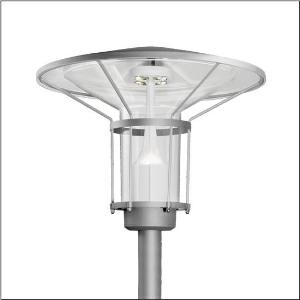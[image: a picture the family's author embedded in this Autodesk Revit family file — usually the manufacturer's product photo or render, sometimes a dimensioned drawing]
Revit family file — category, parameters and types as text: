
# Revit family: laterne_classic_iq___pl1_2s_5xa5245of14h_0553
name_source: partatom
category: Lighting Fixtures
units: mm (PartAtom-declared; Revit-internal decimal feet)

## family parameters
Cut with Voids When Loaded = No
Host = Face
Light Source = No
Part Type = Normal
Room Calculation Point = No
Round Connector Dimension = Use Diameter
Shared = No

## types (1)
- --- (1 x LED, 2670 lm, 21.8 W, 2700K)
    Apparent Load = 22 VA
    CIE Flux Codes = 21 60 93 97 100
    Color Rendering = 70
    Color Temperature = 2700K
    Default Elevation = 1800 mm
    Description = Lantern Classic iQ, mast luminaire, Module 540 iQ-SR, primary light control with 3 zone facetted reflector, of plastic, silver coated, highly specular, structured, primary optical cover: cover, of PMMA, transparent, light distribution: PL1.2s, light emission: direct distribution, primary light characteristic: symmetric, installation type: post-top, LED, High Power LED, rated luminous flux: 2.970lm, luminous efficacy: 136lm/W, light colour: 727, colour temperature: 2700K, control gear: ECG iQ, control: pre-setting: logarithmic dimming characteristic, Street-Remote, Auto-Match, Temp-Guard, Lumen-Switch, Night-Set, Smart-Wire, Light-Fading, Desk-Remote (wireless, voltage-free reading and setting of iQ features in the workshop via application-optimized NFC function/RFID function), optimised constant luminous flux control (CLO 2.0), with terminal, 6-pole, max. 2.5mm², mains connection: 230..240V, AC, 50/60Hz, start of lifetime: 22W, end of service life: 23W, reduction: 11W, luminaire housing, upper part, of glass-fibre reinforced polyester, coated, Siteco® metallic grey (DB 702S), diameter: 750mm, height: 596mm, spigot size: d x l = 76 x 70mm (post-top) | with reducer (optional accessory) 60 x 70mm, post-top mast mounting element, of diecast aluminium, coated, Siteco® metallic grey (DB 702S), Module 540 iQ-SR, traffic white (RAL 9016), equipment: standard, protection rating (complete): IP65, insulation class (complete): insulation class II (safety insulation), certification: CE, ENEC, VDE, packaging unit: 1 piece

Light Distribution: PL1.2s
    Height = 596 mm
    Lamp = 1 x LED
    Lamp Light Flux = 2670 lm
    Lamp Power = 21.8 W
    Lamp count = 1
    Length = 750 mm
    Luminous efficacy = 122 lm/W
    Manufacturer = Siteco
    ModVariant = No
    Model = 5XA5245OF14H
    Number of Poles = 1
    OnlyDefault = Yes
    Power Factor = 1
    Product Name = Laterne Classic iQ | PL1.2s
    Product group = mast luminaire | pylon top
    ProductGroupID = 6100
    Protection Class = Protection class II
    Protection Degree = IP 65
    RLX_Detail_Level = 1
    RLX_Emergency_Light_Flux = 0 lm
    RLX_Emergency_Type = 0
    RLX_Emergency_Type_DB = No
    RlxData = <blob elided: 62337 chars, md5=af5ee4c5>
    Socket = socket
    Standby Power = 0 W
    System Light Flux = 2670 lm
    System Power = 22 W
    Type Comments = factory setting: luminous flux: 100 % | dim-lin: 254 | 456 mA
    Type Image = l_1006052.jpg
    URL = http://relux.com
    VarID = @adj_115561
    Voltage = 0 V
    Weight = 0.00 kg
    Width = 0 mm  [stored 0 ft]

note: [stored X ft] marks values corroborated as IEEE doubles in the binary element streams (Revit-internal decimal feet)

## geometry (parser evidence)
native form markers: Blend x4, Sweep x9
no freeform markers — native parametric forms only
